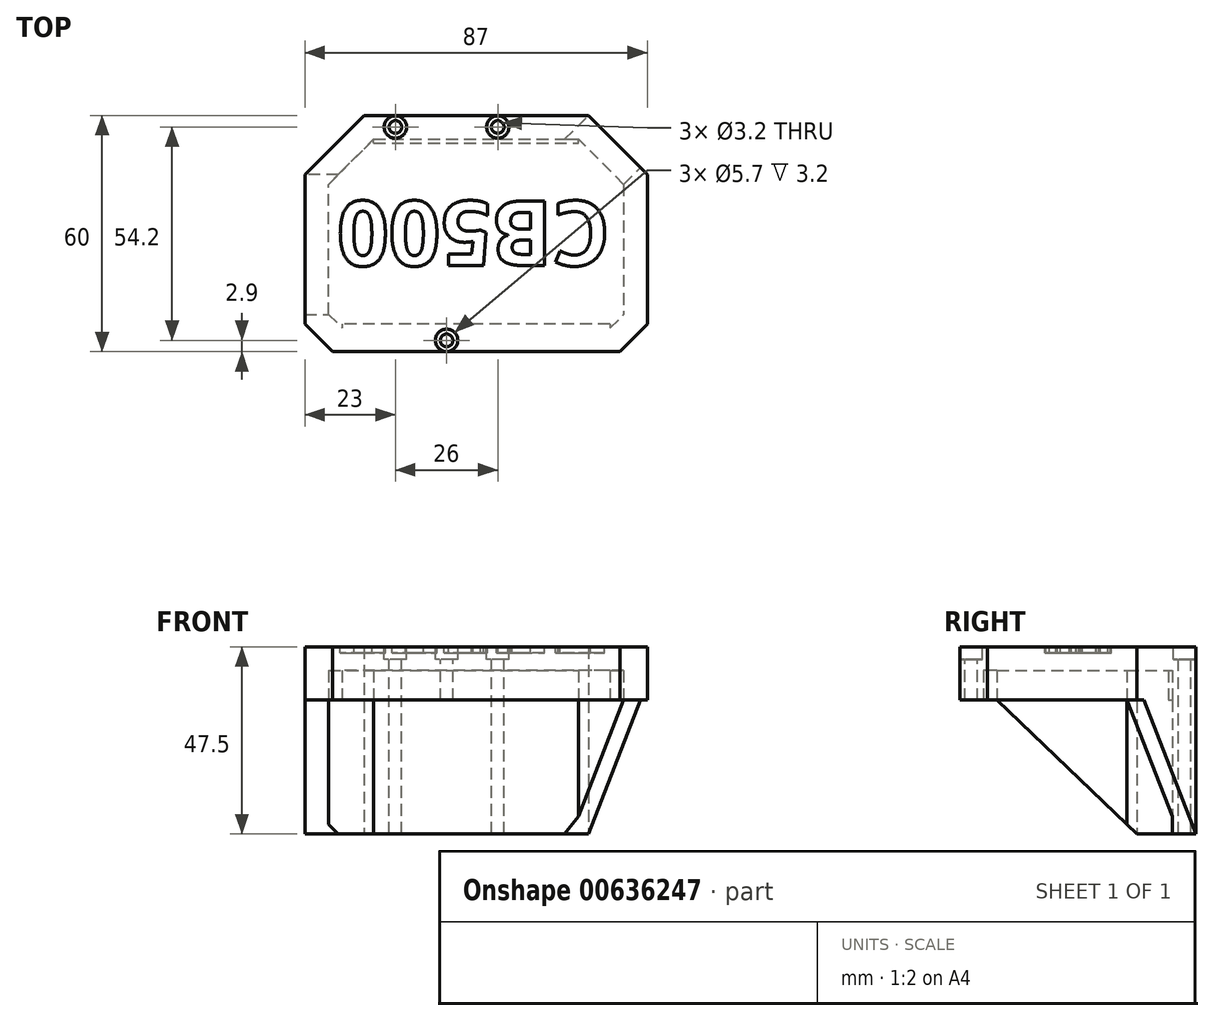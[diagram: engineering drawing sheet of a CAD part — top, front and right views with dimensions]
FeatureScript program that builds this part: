
annotation { "Feature Type Name" : "Feature", "Feature Type Description" : "" }
export const myFeature = defineFeature(function(context is Context, id is Id, definition is map)
    precondition{}
    {
        {
            var Q0;
            Q0=qCreatedBy(makeId("Top.planeOp"),FACE);
            var sketch = newSketch(context, id + "F0", { "sketchPlane" : qUnion([Q0])});
            skLineSegment(sketch, "E0.bottom", {"start": v(0, 0) * mm, "end": v(-87, 0) * mm, "construction": true});
            skLineSegment(sketch, "E0.top", {"start": v(0, 60) * mm, "end": v(-87, 60) * mm, "construction": true});
            skLineSegment(sketch, "E0.left", {"start": v(0, 0) * mm, "end": v(0, 60) * mm, "construction": true});
            skLineSegment(sketch, "E0.right", {"start": v(-87, 0) * mm, "end": v(-87, 60) * mm, "construction": true});
            skLineSegment(sketch, "E1", {"start": v(-87, 7) * mm, "end": v(-80, 0) * mm});
            skLineSegment(sketch, "E2", {"start": v(-7, 0) * mm, "end": v(0, 7) * mm});
            skLineSegment(sketch, "E3", {"start": v(0, 45) * mm, "end": v(-15, 60) * mm});
            skLineSegment(sketch, "E4", {"start": v(-87, 45) * mm, "end": v(-72, 60) * mm});
            skLineSegment(sketch, "E5", {"start": v(-72, 60) * mm, "end": v(-15, 60) * mm});
            skLineSegment(sketch, "E6", {"start": v(0, 45) * mm, "end": v(0, 7) * mm});
            skLineSegment(sketch, "E7", {"start": v(-7, 0) * mm, "end": v(-80, 0) * mm});
            skLineSegment(sketch, "E8", {"start": v(-87, 7) * mm, "end": v(-87, 45) * mm});
            skSolve(sketch);
        }
        {
            var Q0;
            Q0 = qSketchRegion(id + "F0", true);
            extrude(context, id + "F1", {"entities" : qUnion([Q0]), "depth" : 13.5 * mm, "offsetDistance" : 25 * mm});
        }
        {
            var Q0;
            Q0=makeQuery(id+"F1.opExtrude","CAP_FACE",FACE,{"disambiguationData":[OSD([sQuery(id+"F0.wireOp",EDGE,"E1"),sQuery(id+"F0.wireOp",EDGE,"E2"),sQuery(id+"F0.wireOp",EDGE,"E3"),sQuery(id+"F0.wireOp",EDGE,"E4"),sQuery(id+"F0.wireOp",EDGE,"E5"),sQuery(id+"F0.wireOp",EDGE,"E6"),sQuery(id+"F0.wireOp",EDGE,"E7"),sQuery(id+"F0.wireOp",EDGE,"E8")])],"isStart":true});
            shell(context, id + "F2", {"entities" : qUnion([Q0]), "thickness" : 6 * mm});
        }
        {
            var Q0;
            Q0=makeQuery(id+"F1.opExtrude","CAP_FACE",FACE,{"disambiguationData":[OSD([sQuery(id+"F0.wireOp",EDGE,"E1"),sQuery(id+"F0.wireOp",EDGE,"E2"),sQuery(id+"F0.wireOp",EDGE,"E3"),sQuery(id+"F0.wireOp",EDGE,"E4"),sQuery(id+"F0.wireOp",EDGE,"E5"),sQuery(id+"F0.wireOp",EDGE,"E6"),sQuery(id+"F0.wireOp",EDGE,"E7"),sQuery(id+"F0.wireOp",EDGE,"E8")])],"isStart":true});
            var sketch = newSketch(context, id + "F3", { "sketchPlane" : qUnion([Q0])});
            skLineSegment(sketch, "E9", {"start": v(-81, -9.49) * mm, "end": v(-81, -42.51) * mm});
            skLineSegment(sketch, "E10", {"start": v(-81, -42.51) * mm, "end": v(-69.51, -54) * mm});
            skLineSegment(sketch, "E11", {"start": v(-69.51, -54) * mm, "end": v(-17.49, -54) * mm});
            skLineSegment(sketch, "E12", {"start": v(-17.49, -54) * mm, "end": v(-6, -42.51) * mm});
            skLineSegment(sketch, "E13", {"start": v(-6, -42.51) * mm, "end": v(-1.76, -46.76) * mm});
            skLineSegment(sketch, "E14", {"start": v(-1.76, -46.76) * mm, "end": v(-15, -60) * mm});
            skLineSegment(sketch, "E15", {"start": v(-15, -60) * mm, "end": v(-72, -60) * mm});
            skLineSegment(sketch, "E16", {"start": v(-72, -60) * mm, "end": v(-87, -45) * mm});
            skLineSegment(sketch, "E17", {"start": v(-87, -45) * mm, "end": v(-87, -9.49) * mm});
            skLineSegment(sketch, "E18", {"start": v(-87, -9.49) * mm, "end": v(-81, -9.49) * mm});
            skSolve(sketch);
        }
        {
            var Q0;
            Q0 = qSketchRegion(id + "F3", true);
            extrude(context, id + "F4", {"entities" : qUnion([Q0]), "operationType" : NewBodyOperationType.ADD, "depth" : 34 * mm, "offsetDistance" : 25 * mm});
        }
        {
            var Q0;
            Q0=qCreatedBy(makeId("Top.planeOp"),FACE);
            cPlane(context, id + "F5", {"entities" : qUnion([Q0]), "cplaneType" : CPlaneType.OFFSET, "offset" : 34 * mm, "oppositeDirection" : true, "width" : 150 * mm, "height" : 150 * mm});
        }
        {
            var Q0;
            Q0=makeQuery(id+"F1.opExtrude","CAP_FACE",FACE,{"disambiguationData":[OSD([sQuery(id+"F0.wireOp",EDGE,"E1"),sQuery(id+"F0.wireOp",EDGE,"E2"),sQuery(id+"F0.wireOp",EDGE,"E3"),sQuery(id+"F0.wireOp",EDGE,"E4"),sQuery(id+"F0.wireOp",EDGE,"E5"),sQuery(id+"F0.wireOp",EDGE,"E6"),sQuery(id+"F0.wireOp",EDGE,"E7"),sQuery(id+"F0.wireOp",EDGE,"E8")])],"isStart":false});
            var sketch = newSketch(context, id + "F6", { "sketchPlane" : qUnion([Q0])});
            skCircle(sketch, "E19", {"center": v(-38, 57.1) * mm, "radius": 1.6 * mm});
            skCircle(sketch, "E20", {"center": v(-64, 57.1) * mm, "radius": 1.6 * mm});
            skCircle(sketch, "E21", {"center": v(-51, 2.9) * mm, "radius": 1.6 * mm});
            skPoint(sketch, "E22", {"position": v(-51, 57.1) * mm});
            skSolve(sketch);
        }
        {
            var Q0;
            Q0 = qSketchRegion(id + "F6", true);
            extrude(context, id + "F7", {"entities" : qUnion([Q0]), "operationType" : NewBodyOperationType.REMOVE, "oppositeDirection" : true, "depth" : 60 * mm, "offsetDistance" : 25 * mm});
        }
        {
            var Q0;
            Q0=makeQuery(id+"F4.boolean.opBoolean","MERGE",FACE,{"derivedFrom":[makeQuery(id+"F1.opExtrude","SWEPT_FACE",FACE,{"disambiguationData":[OSD([sQuery(id+"F0.wireOp",EDGE,"E8")])]}),makeQuery(id+"F4.opExtrude","SWEPT_FACE",FACE,{"disambiguationData":[OSD([sQuery(id+"F3.wireOp",EDGE,"E17")])]})]});
            var sketch = newSketch(context, id + "F8", { "sketchPlane" : qUnion([Q0])});
            skLineSegment(sketch, "E23", {"start": v(-9.49, 0) * mm, "end": v(-45, -34) * mm});
            skLineSegment(sketch, "E24", {"start": v(-45, -34) * mm, "end": v(-9.49, -34) * mm});
            skLineSegment(sketch, "E25", {"start": v(-9.49, -34) * mm, "end": v(-9.49, 0) * mm});
            skSolve(sketch);
        }
        {
            var Q0;
            Q0 = qSketchRegion(id + "F8", true);
            extrude(context, id + "F9", {"entities" : qUnion([Q0]), "operationType" : NewBodyOperationType.REMOVE, "endBound" : BoundingType.UP_TO_NEXT, "oppositeDirection" : true, "depth" : 25 * mm, "offsetDistance" : 25 * mm});
        }
        {
            var Q0;
            Q0=makeQuery(id+"F1.opExtrude","CAP_FACE",FACE,{"disambiguationData":[OSD([sQuery(id+"F0.wireOp",EDGE,"E1"),sQuery(id+"F0.wireOp",EDGE,"E2"),sQuery(id+"F0.wireOp",EDGE,"E3"),sQuery(id+"F0.wireOp",EDGE,"E4"),sQuery(id+"F0.wireOp",EDGE,"E5"),sQuery(id+"F0.wireOp",EDGE,"E6"),sQuery(id+"F0.wireOp",EDGE,"E7"),sQuery(id+"F0.wireOp",EDGE,"E8")])],"isStart":false});
            var sketch = newSketch(context, id + "F10", { "sketchPlane" : qUnion([Q0])});
            skCircle(sketch, "E26", {"center": v(-64, 57.1) * mm, "radius": 2.85 * mm});
            skCircle(sketch, "E27", {"center": v(-38, 57.1) * mm, "radius": 2.85 * mm});
            skCircle(sketch, "E28", {"center": v(-51, 2.9) * mm, "radius": 2.85 * mm});
            skSolve(sketch);
        }
        {
            var Q0;
            Q0 = qSketchRegion(id + "F10", true);
            extrude(context, id + "F11", {"entities" : qUnion([Q0]), "operationType" : NewBodyOperationType.REMOVE, "oppositeDirection" : true, "depth" : 3.2 * mm, "offsetDistance" : 25 * mm});
        }
        {
            var Q0;
            Q0=makeQuery(id+"F1.opExtrude","CAP_FACE",FACE,{"disambiguationData":[OSD([sQuery(id+"F0.wireOp",EDGE,"E1"),sQuery(id+"F0.wireOp",EDGE,"E2"),sQuery(id+"F0.wireOp",EDGE,"E3"),sQuery(id+"F0.wireOp",EDGE,"E4"),sQuery(id+"F0.wireOp",EDGE,"E5"),sQuery(id+"F0.wireOp",EDGE,"E6"),sQuery(id+"F0.wireOp",EDGE,"E7"),sQuery(id+"F0.wireOp",EDGE,"E8")])],"isStart":false});
            var sketch = newSketch(context, id + "F12", { "sketchPlane" : qUnion([Q0])});
            skText(sketch, "E29", { "text": "CB500", "fontName": "OpenSans-Bold.ttf"});
            const initialGuessF12  = {"E29": [-0.0095, 0.03827, -1, 0, 0.01652]};
            skSetInitialGuess(sketch, initialGuessF12);
            skSolve(sketch);
        }
        {
            var Q0;
            Q0 = qSketchRegion(id + "F12", true);
            extrude(context, id + "F13", {"entities" : qUnion([Q0]), "operationType" : NewBodyOperationType.REMOVE, "oppositeDirection" : true, "depth" : 1.5 * mm, "offsetDistance" : 25 * mm});
        }
        {
            var Q0;
            Q0=makeQuery(id+"F4.boolean.opBoolean","MERGE",FACE,{"derivedFrom":[makeQuery(id+"F1.opExtrude","SWEPT_FACE",FACE,{"disambiguationData":[OSD([sQuery(id+"F0.wireOp",EDGE,"E3")])]}),makeQuery(id+"F4.opExtrude","SWEPT_FACE",FACE,{"disambiguationData":[OSD([sQuery(id+"F3.wireOp",EDGE,"E14")])]})]});
            var sketch = newSketch(context, id + "F14", { "sketchPlane" : qUnion([Q0])});
            skLineSegment(sketch, "E30", {"start": v(34.3, 0) * mm, "end": v(53.03, -34) * mm});
            skLineSegment(sketch, "E31", {"start": v(53.03, -34) * mm, "end": v(31.82, -34) * mm});
            skLineSegment(sketch, "E32", {"start": v(31.82, -34) * mm, "end": v(31.82, 0) * mm});
            skLineSegment(sketch, "E33", {"start": v(31.82, 0) * mm, "end": v(34.3, 0) * mm});
            skSolve(sketch);
        }
        {
            var Q0;
            Q0 = qSketchRegion(id + "F14", true);
            extrude(context, id + "F15", {"entities" : qUnion([Q0]), "operationType" : NewBodyOperationType.REMOVE, "endBound" : BoundingType.UP_TO_NEXT, "oppositeDirection" : true, "depth" : 25 * mm, "offsetDistance" : 25 * mm});
        }
        {
            var Q0;
            Q0=makeQuery(id+"F4.boolean.opBoolean","MERGE",FACE,{"derivedFrom":[makeQuery(id+"F2.opShell","OFFSET_FACE",FACE,{"disambiguationData":[OSD([sQuery(id+"F0.wireOp",EDGE,"E5")])]}),makeQuery(id+"F4.opExtrude","SWEPT_FACE",FACE,{"disambiguationData":[OSD([sQuery(id+"F3.wireOp",EDGE,"E11")])]})]});
            var sketch = newSketch(context, id + "F16", { "sketchPlane" : qUnion([Q0])});
            skLineSegment(sketch, "E34.bottom", {"start": v(-69.51, 7.5) * mm, "end": v(-17.49, 7.5) * mm});
            skLineSegment(sketch, "E34.top", {"start": v(-69.51, 0) * mm, "end": v(-17.49, 0) * mm});
            skLineSegment(sketch, "E34.left", {"start": v(-69.51, 7.5) * mm, "end": v(-69.51, 0) * mm});
            skLineSegment(sketch, "E34.right", {"start": v(-17.49, 7.5) * mm, "end": v(-17.49, 0) * mm});
            skSolve(sketch);
        }
        {
            var Q0;
            Q0 = qSketchRegion(id + "F16", true);
            extrude(context, id + "F17", {"entities" : qUnion([Q0]), "operationType" : NewBodyOperationType.ADD, "depth" : 1 * mm, "offsetDistance" : 25 * mm});
        }
        {
            var Q0;
            Q0=makeQuery(id+"F2.opShell","OFFSET_FACE",FACE,{"disambiguationData":[OSD([sQuery(id+"F0.wireOp",EDGE,"E7")])]});
            var sketch = newSketch(context, id + "F18", { "sketchPlane" : qUnion([Q0])});
            skLineSegment(sketch, "E35.bottom", {"start": v(9.49, 7.5) * mm, "end": v(77.51, 7.5) * mm});
            skLineSegment(sketch, "E35.top", {"start": v(9.49, 0) * mm, "end": v(77.51, 0) * mm});
            skLineSegment(sketch, "E35.left", {"start": v(9.49, 7.5) * mm, "end": v(9.49, 0) * mm});
            skLineSegment(sketch, "E35.right", {"start": v(77.51, 7.5) * mm, "end": v(77.51, 0) * mm});
            skSolve(sketch);
        }
        {
            var Q0;
            Q0 = qSketchRegion(id + "F18", true);
            extrude(context, id + "F19", {"entities" : qUnion([Q0]), "operationType" : NewBodyOperationType.ADD, "depth" : 1 * mm, "offsetDistance" : 25 * mm});
        }
    });
